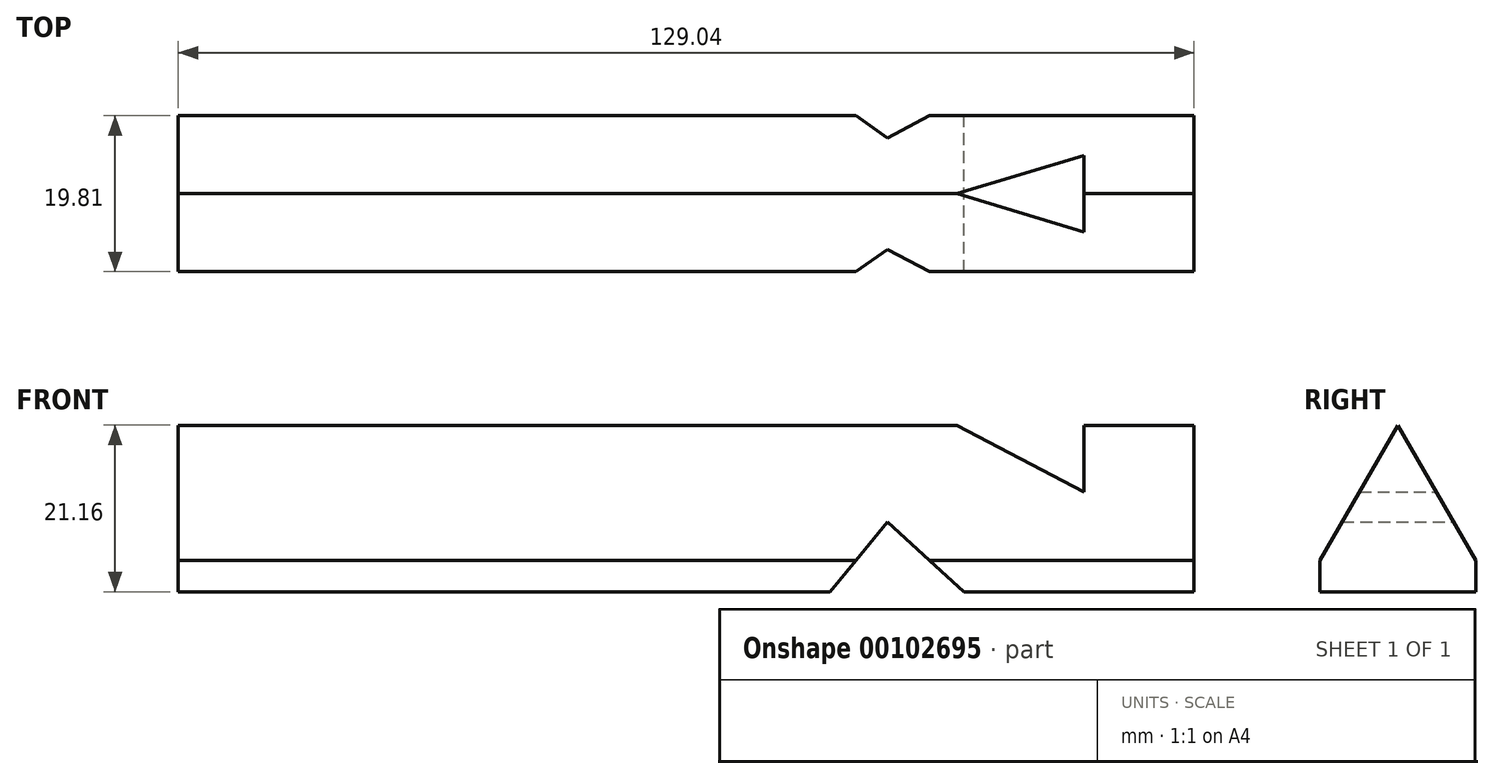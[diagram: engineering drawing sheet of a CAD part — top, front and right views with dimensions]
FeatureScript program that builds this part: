
annotation { "Feature Type Name" : "Feature", "Feature Type Description" : "" }
export const myFeature = defineFeature(function(context is Context, id is Id, definition is map)
    precondition{}
    {
        {
            var Q0;
            Q0=qCreatedBy(makeId("Front.planeOp"),FACE);
            var sketch = newSketch(context, id + "F0", { "sketchPlane" : qUnion([Q0])});
            skLineSegment(sketch, "E0.bottom", {"start": v(64.52, 10.8) * mm, "end": v(-64.52, 10.8) * mm});
            skLineSegment(sketch, "E0.top", {"start": v(64.52, -10.8) * mm, "end": v(-64.52, -10.8) * mm});
            skLineSegment(sketch, "E0.left", {"start": v(64.52, 10.8) * mm, "end": v(64.52, -10.8) * mm});
            skLineSegment(sketch, "E0.right", {"start": v(-64.52, 10.8) * mm, "end": v(-64.52, -10.8) * mm});
            skPoint(sketch, "E0.middle", {"position": v(0, 0) * mm});
            skLineSegment(sketch, "E1", {"start": v(50.55, 10.8) * mm, "end": v(50.55, -10.8) * mm});
            skLineSegment(sketch, "E2", {"start": v(35.3, 10.8) * mm, "end": v(35.3, -10.8) * mm});
            skLineSegment(sketch, "E3", {"start": v(35.3, -10.8) * mm, "end": v(25.55, -1.9) * mm});
            skLineSegment(sketch, "E4", {"start": v(25.55, -1.9) * mm, "end": v(18.29, -10.8) * mm});
            skLineSegment(sketch, "E5", {"start": v(50.55, 1.9) * mm, "end": v(35.3, 9.87) * mm});
            skLineSegment(sketch, "E6", {"start": v(35.3, 9.87) * mm, "end": v(35.3, 9.87) * mm});
            skLineSegment(sketch, "E7", {"start": v(35.3, 9.87) * mm, "end": v(33.53, 10.8) * mm});
            skSolve(sketch);
        }
        {
            var Q0;
            {var subQ4=sQuery(id+"F0.wireOp",EDGE,"E0.right");Q0=makeQuery(id+"F0.imprint","IMPRINT",FACE,{"disambiguationData":[TD([[makeQuery(id+"F0.imprint","IMPRINT",EDGE,{"derivedFrom":subQ4}),1.0]])]});}
            var Q1;
            {var subQ5=sQuery(id+"F0.wireOp",EDGE,"E5");Q1=makeQuery(id+"F0.imprint","IMPRINT",FACE,{"disambiguationData":[TD([[makeQuery(id+"F0.imprint","IMPRINT",EDGE,{"derivedFrom":subQ5}),1.0]])]});}
            var Q2;
            {var subQ4=sQuery(id+"F0.wireOp",EDGE,"E0.left");Q2=makeQuery(id+"F0.imprint","IMPRINT",FACE,{"disambiguationData":[TD([[makeQuery(id+"F0.imprint","IMPRINT",EDGE,{"derivedFrom":subQ4}),-1.0]])]});}
            extrude(context, id + "F1", {"entities" : qUnion([Q0, Q1, Q2]), "depth" : 19.8 * mm});
        }
        {
            var Q0;
            {var subQ0=sQuery(id+"F0.wireOp",EDGE,"E0.bottom");Q0=makeQuery(id+"F1.opExtrude","CAP_EDGE",EDGE,{"disambiguationData":[OSD([subQ0]),TDD([makeQuery(id+"F0.imprint","IMPRINT",EDGE,{"disambiguationData":[TD([[makeQuery(id+"F0.imprint","INTERSECT",VERTEX,{"derivedFrom":[subQ0,sQuery(id+"F0.wireOp",EDGE,"E0.right")]}),1.0]])],"derivedFrom":subQ0})])],"isStart":false});}
            chamfer(context, id + "F2", {"entities" : qUnion([Q0]), "chamferType" : ChamferType.OFFSET_ANGLE, "width" : 10.16 * mm, "oppositeDirection" : true, "angle" : 60 * degree, "tangentPropagation" : true});
        }
        {
            var Q0;
            {var subQ0=sQuery(id+"F0.wireOp",EDGE,"E0.bottom");Q0=makeQuery(id+"F1.opExtrude","CAP_EDGE",EDGE,{"disambiguationData":[OSD([subQ0]),TDD([makeQuery(id+"F0.imprint","IMPRINT",EDGE,{"disambiguationData":[TD([[makeQuery(id+"F0.imprint","INTERSECT",VERTEX,{"derivedFrom":[subQ0,sQuery(id+"F0.wireOp",EDGE,"E0.right")]}),1.0]])],"derivedFrom":subQ0})])],"isStart":true});}
            chamfer(context, id + "F3", {"entities" : qUnion([Q0]), "chamferType" : ChamferType.OFFSET_ANGLE, "width" : 10.16 * mm, "oppositeDirection" : false, "angle" : 60 * degree, "tangentPropagation" : true});
        }
    });
